# Revit family: Electronics_Commercial-Loudspeakers_Biamp_Sphere-Loudspeaker_EN-SPH6T20-W
name_source: partatom
category: Communication Devices
units: mm (PartAtom-declared; Revit-internal decimal feet)

## family parameters
Cut with Voids When Loaded = No
Host = Face
Maintain Annotation Orientation = No
OmniClass Number = 23.85.10.11.14.14.14
OmniClass Title = Loudspeakers
Part Type = Normal
Room Calculation Point = No
Round Connector Dimension = Use Diameter
Shared = No

## types (1)
- EN-SPH6T20-W
    100V transformer power taps in watts = 20 - 15 - 10 - 5 - 2.5
    Certificate ref = 1438/CPR/0353
    Closest RAL colour (subject to deviations) = RAL9010
    Colour = White
    Connector Description = Conductor; 20-15-10-5-2.5 W 100V
    Default Elevation = 48 "
    Depth = 10 "
    Description = EN-SPH6T20-W EN54-24 Certified 6 Sphere Loudspeaker
    Diameter = 10 "
    Frequency response in Hz = 90 - 20 k
    Grill Material = Biamp - Plastic - White(Grid)
    Housing Material = Biamp - Plastic - White
    IP rating = 35
    Loudspeaker system = Full range
    Low impedance dynamic power in watts = 20
    Main construction material = ABS plastic
    Manufacturer = Biamp
    Max SPL 1m in dB = 106,5
    Model = EN-SPH6T20-W
    Mounting system = 2 screws
    Operating temperatures = -20°C to +80°C
    Product Documentation Link = https://downloads.biamp.com
    Product Page URL = https://www.biamp.com
    Product data url = https://bimobject.com
    SPL 1W/1m in dB = 93,5
    URL = https://www.biamp.com
    Version = 1
    Vertical dispersion angle 1000 Hz = 180°
    Weight = 4.74 lb
    Woofer cone material = Paper
    Woofer size in inch = 6.5

## geometry (parser evidence)
native form markers: Sweep x2
no freeform markers — native parametric forms only
